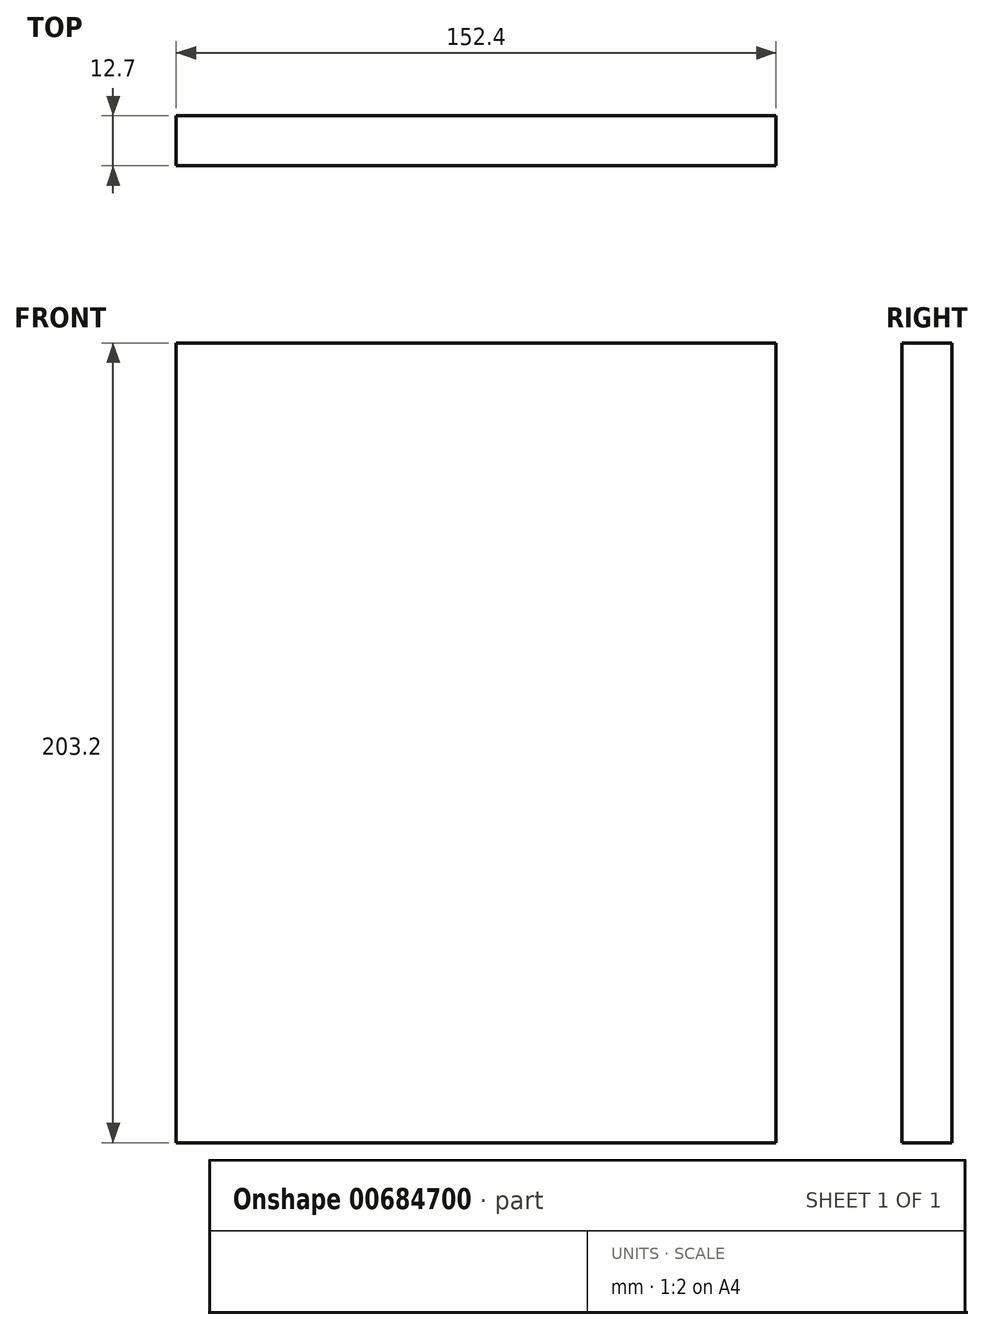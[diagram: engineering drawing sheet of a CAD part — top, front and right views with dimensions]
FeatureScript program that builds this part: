
annotation { "Feature Type Name" : "Feature", "Feature Type Description" : "" }
export const myFeature = defineFeature(function(context is Context, id is Id, definition is map)
    precondition{}
    {
        {
            var Q0;
            Q0=qCreatedBy(makeId("Front.planeOp"),FACE);
            var sketch = newSketch(context, id + "F0", { "sketchPlane" : qUnion([Q0])});
            skLineSegment(sketch, "E0.bottom", {"start": v(-104.15, 99.33) * mm, "end": v(48.25, 99.33) * mm});
            skLineSegment(sketch, "E0.top", {"start": v(-104.15, -103.87) * mm, "end": v(48.25, -103.87) * mm});
            skLineSegment(sketch, "E0.left", {"start": v(-104.15, 99.33) * mm, "end": v(-104.15, -103.87) * mm});
            skLineSegment(sketch, "E0.right", {"start": v(48.25, 99.33) * mm, "end": v(48.25, -103.87) * mm});
            skSolve(sketch);
        }
        {
            var Q0;
            Q0=qSketchRegion(id+"F0",true);
            extrude(context, id + "F1", {"entities" : qUnion([Q0]), "depth" : 12.7 * mm, "offsetDistance" : 25.4 * mm});
        }
    });
